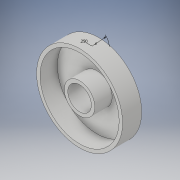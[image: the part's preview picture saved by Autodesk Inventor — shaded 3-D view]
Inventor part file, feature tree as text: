
AUTODESK INVENTOR PART (.ipt)
format: ipt  version: 2017 (Build 210142000, 142)  size: 134,144 bytes
history: native  units: in
note: dims shown in document units (in); Inventor stores cm internally (conversion verified against a paired STEP export)
features: sketch x3, extrude x2, projected_geometry x2
ambient origin geometry x8: Origin, YZ Plane, XZ Plane, XY Plane, X Axis, Y Axis, Z Axis, Center Point
bodies: Solid1 (feature_tree)
feature tree (7):
  extrude  "Extrusion1"  Depth=0.05in
  extrude  "Extrusion3"  Depth=0.05in
  sketch  "Sketch6"  dims[d5=0.275in d6=0.0in d15=0.05in d16=0.0in d17=0.25in]
  sketch  "Sketch1"  dims[d1=0.44in d2=0.05in]
  sketch  "Sketch5"  dims[d3=0.35in d4=0.05in]
  projected_geometry  "Projected Loop2"
  projected_geometry  "Projected Loop3"
